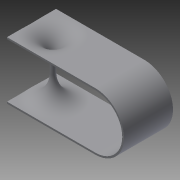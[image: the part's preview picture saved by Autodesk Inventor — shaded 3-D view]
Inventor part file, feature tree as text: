
AUTODESK INVENTOR PART (.ipt)
format: ipt  version: 2013 (Build 170138000, 138)  size: 222,208 bytes
history: native  units: in
note: dims shown in document units (in); Inventor stores cm internally (conversion verified against a paired STEP export)
features: fillet x4, extrude x3, sketch x3
ambient origin geometry x8: Origin, YZ Plane, XZ Plane, XY Plane, X Axis, Y Axis, Z Axis, Center Point
bodies: Solid1 (feature_tree)
feature tree (10):
  extrude  "Extrusion1"  Depth=0.45in TaperAngle=0.0deg
  extrude  "Extrusion2"  Depth=0.1875in
  fillet  "Fillet1"  Radius=1.0in
  fillet  "Fillet2"  Radius=0.1875in
  extrude  "Extrusion3"  [1 undecoded]
  fillet  "Fillet3"  [1 undecoded]
  fillet  "Fillet4"  [1 undecoded]
  sketch  "Sketch1"  dims[d0=0.4in d1=0.0in d2=0.45in d3=0.0in]
  sketch  "Sketch2"  dims[d4=0.1875in d5=0.1875in d6=1.0in d7=0.0in d8=0.1875in]
  sketch  "Sketch3"  dims[d9=0.1875in]
note: 3 required parameter values undecoded (feature->parameter linkage not recoverable at this tier; creation-order binding heuristic only, values carry confidence <= 0.55)
